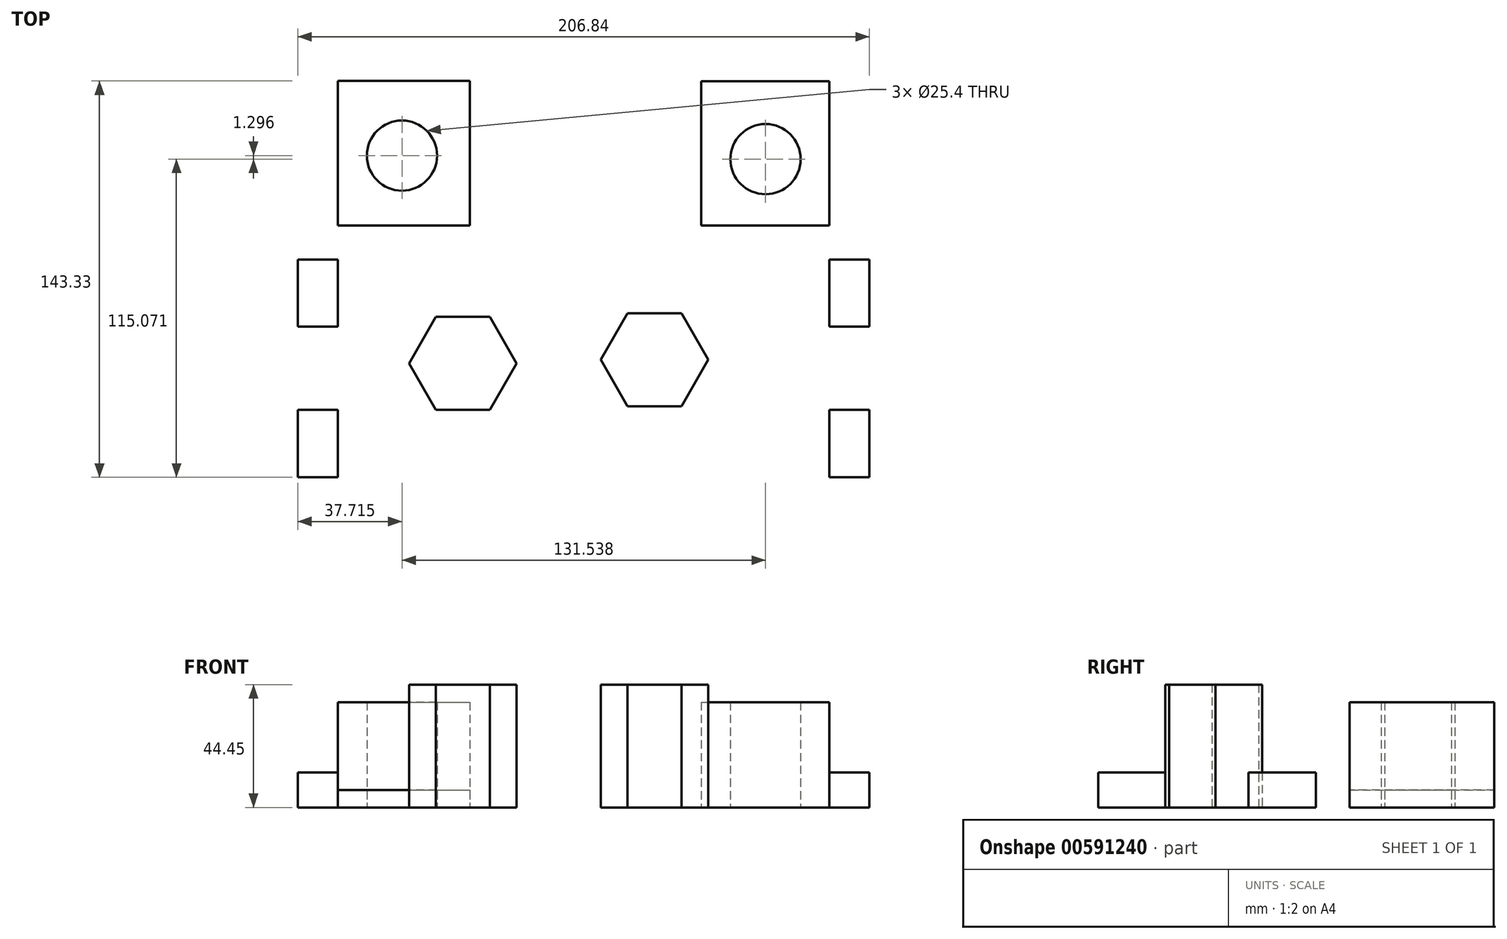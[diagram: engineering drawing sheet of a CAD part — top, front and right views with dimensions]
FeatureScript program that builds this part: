
annotation { "Feature Type Name" : "Feature", "Feature Type Description" : "" }
export const myFeature = defineFeature(function(context is Context, id is Id, definition is map)
    precondition{}
    {
        {
            var Q0;
            Q0=qCreatedBy(makeId("Top.planeOp"),FACE);
            var sketch = newSketch(context, id + "F0", { "sketchPlane" : qUnion([Q0])});
            skLineSegment(sketch, "E0.bottom", {"start": v(-77.62, 136.42) * mm, "end": v(100.18, 136.42) * mm});
            skLineSegment(sketch, "E0.top", {"start": v(-77.62, -41.38) * mm, "end": v(100.18, -41.38) * mm});
            skLineSegment(sketch, "E0.left", {"start": v(-77.62, 136.42) * mm, "end": v(-77.62, -41.38) * mm});
            skLineSegment(sketch, "E0.right", {"start": v(100.18, 136.42) * mm, "end": v(100.18, -41.38) * mm});
            skLineSegment(sketch, "E1.bottom", {"start": v(-77.62, 84.19) * mm, "end": v(-29.8, 84.19) * mm});
            skLineSegment(sketch, "E1.top", {"start": v(-77.62, 136.42) * mm, "end": v(-29.8, 136.42) * mm});
            skLineSegment(sketch, "E1.left", {"start": v(-77.62, 84.19) * mm, "end": v(-77.62, 136.42) * mm});
            skLineSegment(sketch, "E1.right", {"start": v(-29.8, 84.19) * mm, "end": v(-29.8, 136.42) * mm});
            skLineSegment(sketch, "E2.bottom", {"start": v(53.84, 84.11) * mm, "end": v(101.65, 84.11) * mm});
            skLineSegment(sketch, "E2.top", {"start": v(53.84, 136.35) * mm, "end": v(101.65, 136.35) * mm});
            skLineSegment(sketch, "E2.left", {"start": v(53.84, 84.11) * mm, "end": v(53.84, 136.35) * mm});
            skLineSegment(sketch, "E2.right", {"start": v(101.65, 84.11) * mm, "end": v(101.65, 136.35) * mm});
            skCircle(sketch, "E3.cCircle", {"center": v(-32.4, 34.3) * mm, "radius": 16.85 * mm, "construction": true});
            skLineSegment(sketch, "E3.0", {"start": v(-42.12, 51.14) * mm, "end": v(-22.67, 51.14) * mm});
            skLineSegment(sketch, "E3.1", {"start": v(-22.67, 51.14) * mm, "end": v(-12.94, 34.3) * mm});
            skLineSegment(sketch, "E3.2", {"start": v(-12.94, 34.3) * mm, "end": v(-22.67, 17.44) * mm});
            skLineSegment(sketch, "E3.3", {"start": v(-22.67, 17.44) * mm, "end": v(-42.12, 17.44) * mm});
            skLineSegment(sketch, "E3.4", {"start": v(-42.12, 17.44) * mm, "end": v(-51.85, 34.3) * mm});
            skLineSegment(sketch, "E3.5", {"start": v(-51.85, 34.3) * mm, "end": v(-42.12, 51.14) * mm});
            skPoint(sketch, "E3.0.midPoint", {"position": v(-32.4, 51.14) * mm});
            skCircle(sketch, "E4.cCircle", {"center": v(36.94, 35.59) * mm, "radius": 16.85 * mm, "construction": true});
            skLineSegment(sketch, "E4.0", {"start": v(27.21, 52.44) * mm, "end": v(46.67, 52.44) * mm});
            skLineSegment(sketch, "E4.1", {"start": v(46.67, 52.44) * mm, "end": v(56.4, 35.59) * mm});
            skLineSegment(sketch, "E4.2", {"start": v(56.4, 35.59) * mm, "end": v(46.67, 18.74) * mm});
            skLineSegment(sketch, "E4.3", {"start": v(46.67, 18.74) * mm, "end": v(27.21, 18.74) * mm});
            skLineSegment(sketch, "E4.4", {"start": v(27.21, 18.74) * mm, "end": v(17.49, 35.59) * mm});
            skLineSegment(sketch, "E4.5", {"start": v(17.49, 35.59) * mm, "end": v(27.21, 52.44) * mm});
            skPoint(sketch, "E4.0.midPoint", {"position": v(36.94, 52.44) * mm});
            skLineSegment(sketch, "E5.bottom", {"start": v(100.18, 47.52) * mm, "end": v(114.7, 47.52) * mm});
            skLineSegment(sketch, "E5.top", {"start": v(100.18, 71.87) * mm, "end": v(114.7, 71.87) * mm});
            skLineSegment(sketch, "E5.left", {"start": v(100.18, 47.52) * mm, "end": v(100.18, 71.87) * mm});
            skLineSegment(sketch, "E5.right", {"start": v(114.7, 47.52) * mm, "end": v(114.7, 71.87) * mm});
            skLineSegment(sketch, "E6.bottom", {"start": v(-77.62, 71.87) * mm, "end": v(-92.14, 71.87) * mm});
            skLineSegment(sketch, "E6.top", {"start": v(-77.62, 47.52) * mm, "end": v(-92.14, 47.52) * mm});
            skLineSegment(sketch, "E6.right", {"start": v(-92.14, 71.87) * mm, "end": v(-92.14, 47.52) * mm});
            skLineSegment(sketch, "E7.bottom", {"start": v(-77.62, 17.44) * mm, "end": v(-92.14, 17.44) * mm});
            skLineSegment(sketch, "E7.top", {"start": v(-77.62, -6.9) * mm, "end": v(-92.14, -6.9) * mm});
            skLineSegment(sketch, "E7.right", {"start": v(-92.14, 17.44) * mm, "end": v(-92.14, -6.9) * mm});
            skLineSegment(sketch, "E8.bottom", {"start": v(100.18, -6.9) * mm, "end": v(114.7, -6.9) * mm});
            skLineSegment(sketch, "E8.top", {"start": v(100.18, 17.44) * mm, "end": v(114.7, 17.44) * mm});
            skLineSegment(sketch, "E8.right", {"start": v(114.7, -6.9) * mm, "end": v(114.7, 17.44) * mm});
            skCircle(sketch, "E9", {"center": v(-54.43, 109.46) * mm, "radius": 12.7 * mm});
            skCircle(sketch, "E10", {"center": v(77.11, 108.16) * mm, "radius": 12.7 * mm});
            skSolve(sketch);
        }
        {
            var Q0;
            Q0=makeQuery(id+"F0.imprint","IMPRINT",FACE,{"disambiguationData":[TD([[makeQuery(id+"F0.imprint","IMPRINT",EDGE,{"derivedFrom":sQuery(id+"F0.wireOp",EDGE,"E1.bottom")}),1.0]])]});
            var Q1;
            {var subQ0=sQuery(id+"F0.wireOp",EDGE,"E2.left");Q1=makeQuery(id+"F0.imprint","IMPRINT",FACE,{"disambiguationData":[TD([[makeQuery(id+"F0.imprint","IMPRINT",EDGE,{"derivedFrom":subQ0}),-1.0]])]});}
            extrude(context, id + "F1", {"entities" : qUnion([Q0, Q1]), "depth" : 38.1 * mm, "offsetDistance" : 25.4 * mm});
        }
        {
            var Q0;
            Q0=makeQuery(id+"F0.imprint","IMPRINT",FACE,{"disambiguationData":[TD([[makeQuery(id+"F0.imprint","IMPRINT",EDGE,{"derivedFrom":sQuery(id+"F0.wireOp",EDGE,"E3.0")}),-1.0]])]});
            var Q1;
            Q1=makeQuery(id+"F0.imprint","IMPRINT",FACE,{"disambiguationData":[TD([[makeQuery(id+"F0.imprint","IMPRINT",EDGE,{"derivedFrom":sQuery(id+"F0.wireOp",EDGE,"E4.0")}),-1.0]])]});
            extrude(context, id + "F2", {"entities" : qUnion([Q0, Q1]), "depth" : 44.45 * mm, "offsetDistance" : 25.4 * mm});
        }
        {
            var Q0;
            {var subQ13=sQuery(id+"F0.wireOp",EDGE,"E0.bottom");Q0=makeQuery(id+"F0.imprint","IMPRINT",FACE,{"disambiguationData":[TD([[makeQuery(id+"F0.imprint","IMPRINT",EDGE,{"derivedFrom":subQ13}),-1.0]])]});}
            extrude(context, id + "F3", {"entities" : qUnion([Q0]), "depth" : 6.35 * mm, "offsetDistance" : 25.4 * mm});
        }
        {
            var Q0;
            {var subQ0=sQuery(id+"F0.wireOp",EDGE,"E7.bottom");Q0=makeQuery(id+"F0.imprint","IMPRINT",FACE,{"disambiguationData":[TD([[makeQuery(id+"F0.imprint","IMPRINT",EDGE,{"derivedFrom":subQ0}),1.0]])]});}
            var Q1;
            {var subQ0=sQuery(id+"F0.wireOp",EDGE,"E6.bottom");Q1=makeQuery(id+"F0.imprint","IMPRINT",FACE,{"disambiguationData":[TD([[makeQuery(id+"F0.imprint","IMPRINT",EDGE,{"derivedFrom":subQ0}),1.0]])]});}
            var Q2;
            {var subQ0=sQuery(id+"F0.wireOp",EDGE,"E8.bottom");Q2=makeQuery(id+"F0.imprint","IMPRINT",FACE,{"disambiguationData":[TD([[makeQuery(id+"F0.imprint","IMPRINT",EDGE,{"derivedFrom":subQ0}),1.0]])]});}
            var Q3;
            Q3=makeQuery(id+"F0.imprint","IMPRINT",FACE,{"disambiguationData":[TD([[makeQuery(id+"F0.imprint","IMPRINT",EDGE,{"derivedFrom":sQuery(id+"F0.wireOp",EDGE,"E5.bottom")}),1.0]])]});
            extrude(context, id + "F4", {"entities" : qUnion([Q0, Q1, Q2, Q3]), "operationType" : NewBodyOperationType.ADD, "depth" : 12.7 * mm, "offsetDistance" : 25.4 * mm});
        }
    });
